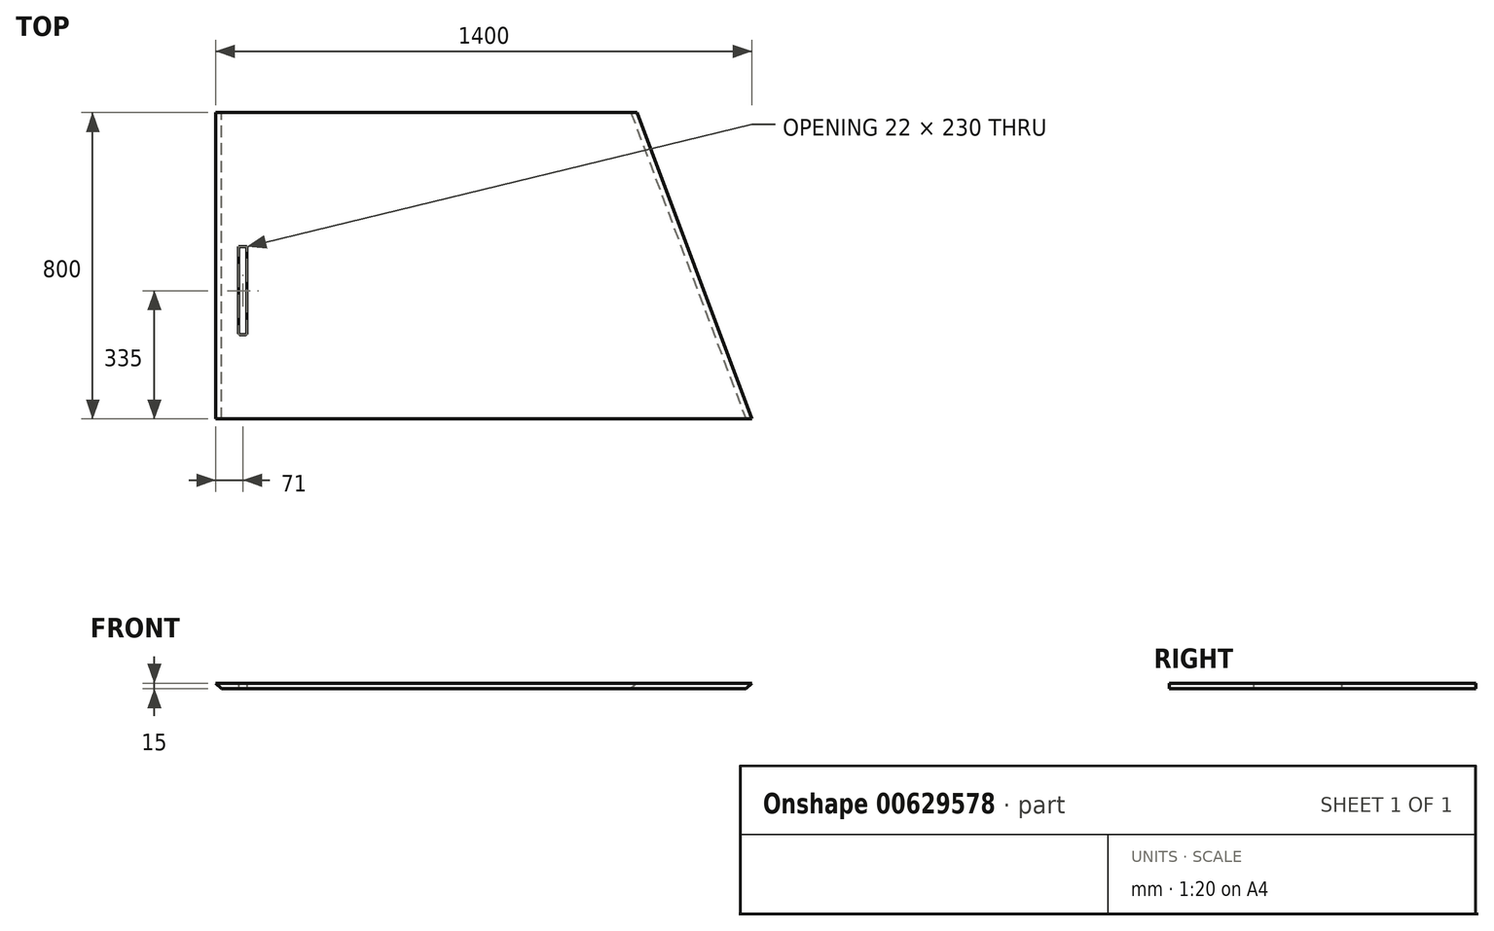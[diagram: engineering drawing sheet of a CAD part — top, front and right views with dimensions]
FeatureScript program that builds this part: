
annotation { "Feature Type Name" : "Feature", "Feature Type Description" : "" }
export const myFeature = defineFeature(function(context is Context, id is Id, definition is map)
    precondition{}
    {
        {
            var Q0;
            Q0=qCreatedBy(makeId("Top.planeOp"),FACE);
            var sketch = newSketch(context, id + "F0", { "sketchPlane" : qUnion([Q0])});
            skLineSegment(sketch, "E0.bottom", {"start": v(-300, 0) * mm, "end": v(-1400, 0) * mm});
            skLineSegment(sketch, "E0.top", {"start": v(0, -800) * mm, "end": v(-1400, -800) * mm});
            skLineSegment(sketch, "E0.left", {"start": v(-300, 0) * mm, "end": v(0, -800) * mm});
            skLineSegment(sketch, "E0.right", {"start": v(-1400, 0) * mm, "end": v(-1400, -800) * mm});
            skLineSegment(sketch, "E1.bottom", {"start": v(-1340, -350) * mm, "end": v(-1318, -350) * mm});
            skLineSegment(sketch, "E1.top", {"start": v(-1335, -580) * mm, "end": v(-1323, -580) * mm});
            skLineSegment(sketch, "E1.left", {"start": v(-1340, -350) * mm, "end": v(-1340, -575) * mm});
            skLineSegment(sketch, "E1.right", {"start": v(-1318, -350) * mm, "end": v(-1318, -575) * mm});
            skPoint(sketch, "E2.visualSharp", {"position": v(-1340, -580) * mm});
            skArc(sketch, "E2.filletArc", {"start": v(-1340, -575) * mm, "mid": v(-1338.54, -578.54) * mm, "end": v(-1335, -580) * mm});
            skPoint(sketch, "E3.visualSharp", {"position": v(-1318, -580) * mm});
            skArc(sketch, "E3.filletArc", {"start": v(-1323, -580) * mm, "mid": v(-1319.46, -578.54) * mm, "end": v(-1318, -575) * mm});
            skSolve(sketch);
        }
        {
            var Q0;
            Q0=makeQuery(id+"F0.imprint","IMPRINT",FACE,{"disambiguationData":[TD([[makeQuery(id+"F0.imprint","IMPRINT",EDGE,{"derivedFrom":sQuery(id+"F0.wireOp",EDGE,"E0.bottom")}),1.0]])]});
            extrude(context, id + "F1", {"entities" : qUnion([Q0]), "depth" : 15 * mm, "offsetDistance" : 25 * mm});
        }
        {
            var Q0;
            Q0=makeQuery(id+"F1.opExtrude","CAP_EDGE",EDGE,{"disambiguationData":[OSD([sQuery(id+"F0.wireOp",EDGE,"E0.right")])],"isStart":true});
            chamfer(context, id + "F2", {"entities" : qUnion([Q0]), "width" : 15 * mm, "tangentPropagation" : true});
        }
        {
            var Q0;
            Q0=makeQuery(id+"F1.opExtrude","CAP_EDGE",EDGE,{"disambiguationData":[OSD([sQuery(id+"F0.wireOp",EDGE,"E0.left")])],"isStart":true});
            chamfer(context, id + "F3", {"entities" : qUnion([Q0]), "width" : 15 * mm, "tangentPropagation" : true});
        }
    });
